# Revit family: Haworth_ExecutiveWoodTablesA5_Rectangular
name_source: partatom
category: Furniture Systems
revit_build: Autodesk Revit 2018 (Build: 20170223_1515(x64)
units: mm (PartAtom-declared; Revit-internal decimal feet)

## family parameters
Always vertical = Yes
Cut with Voids When Loaded = No
OmniClass Number = 23.40.70.14.64.21
OmniClass Title = Systems Furniture
Part Type = Normal
Room Calculation Point = No
Round Connector Dimension = Use Diameter
Shared = No
Work Plane-Based = No

## types (6) — shared parameters
Actual Height = 29 1/2"
Assembly Code = E2020200
Custom Size = No
Manufacturer = Haworth
Max. Depth = 60"
Max. Width = 240"
Min. Depth = 54"
Min. Width = 120"
Model = Haworth Executive Wood Tables A5
Revision Number = 1
Size = Verify Final Dim. w/ Haworth
Standard Depths = 54in or 60in
Standard Widths = 120in - 240in @ 12in increments
Sustainability = https://www.haworth.com
Top Thickness = 1 1/2"
Trim Finish = Haworth _ Glass _ Frosted
URL = https://www.haworth.com
URL - Product = https://www.haworth.com
Warranty = https://www.haworth.com

## per-type parameters (varying)
| type | Actual Depth | Actual Width | Depth | Description | Large | Width |
| 60d 240w | 60" | 240" | 60" | Haworth Executive Wood Tables A5 Rectangular 60d 240w | Yes | 240" |
| 60d 180w | 60" | 180" | 60" | Haworth Executive Wood Tables A5 Rectangular 60d 180w | Yes | 180" |
| 60d 120w | 60" | 120" | 60" | Haworth Executive Wood Tables A5 Rectangular 60d 120w | No | 120" |
| 54d 120w | 54" | 120" | 54" | Haworth Executive Wood Tables A5 Rectangular 54d 120w | No | 120" |
| 54d 180w | 54" | 180" | 54" | Haworth Executive Wood Tables A5 Rectangular 54d 180w | Yes | 180" |
| 54d 240w | 54" | 240" | 54" | Haworth Executive Wood Tables A5 Rectangular 54d 240w | Yes | 240" |

## geometry (parser evidence)
native form markers: Sweep x4
no freeform markers — native parametric forms only
